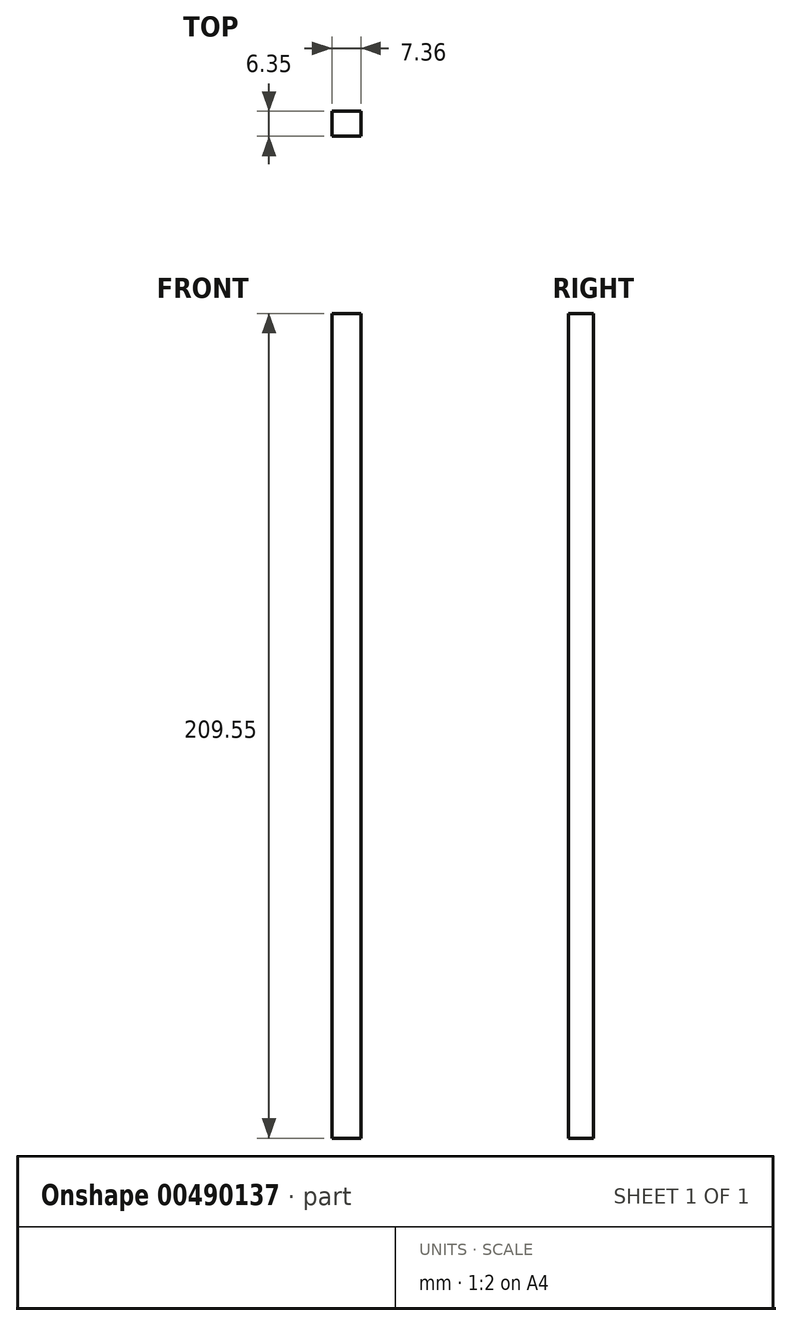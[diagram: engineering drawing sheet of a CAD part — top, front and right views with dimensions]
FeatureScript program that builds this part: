
annotation { "Feature Type Name" : "Feature", "Feature Type Description" : "" }
export const myFeature = defineFeature(function(context is Context, id is Id, definition is map)
    precondition{}
    {
        {
            var Q0;
            Q0=qCreatedBy(makeId("Front.planeOp"),FACE);
            var sketch = newSketch(context, id + "F0", { "sketchPlane" : qUnion([Q0])});
            skLineSegment(sketch, "E0.bottom", {"start": v(-56.35, 190.52) * mm, "end": v(-48.99, 190.52) * mm});
            skLineSegment(sketch, "E0.top", {"start": v(-56.35, -19.03) * mm, "end": v(-48.99, -19.03) * mm});
            skLineSegment(sketch, "E0.left", {"start": v(-56.35, 190.52) * mm, "end": v(-56.35, -19.03) * mm});
            skLineSegment(sketch, "E0.right", {"start": v(-48.99, 190.52) * mm, "end": v(-48.99, -19.03) * mm});
            skSolve(sketch);
        }
        {
            var Q0;
            Q0=makeQuery(id+"F0.imprint","IMPRINT",FACE,{"disambiguationData":[TD([[makeQuery(id+"F0.imprint","IMPRINT",EDGE,{"derivedFrom":sQuery(id+"F0.wireOp",EDGE,"E0.bottom")}),-1.0]])]});
            extrude(context, id + "F1", {"entities" : qUnion([Q0]), "depth" : 6.35 * mm});
        }
    });
